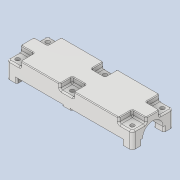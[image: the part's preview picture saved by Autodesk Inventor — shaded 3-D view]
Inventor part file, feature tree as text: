
AUTODESK INVENTOR PART (.ipt)
format: ipt  version: 2020.4 (Build 244396000, 396)  size: 785,920 bytes
history: native  units: mm
features: sketch x15, extrude x14, projected_geometry x10, fillet x3, other x1, mirror x1, boolean_combine x1
ambient origin geometry x8: Origin, YZ Plane, XZ Plane, XY Plane, X Axis, Y Axis, Z Axis, Center Point
bodies: Volumenkörper1 (feature_tree), Solid2 (feature_tree), Solid3 (feature_tree)
feature tree (45):
  extrude  "Extrusion1"  Depth=6.0mm
  other  "Spirale1"
  mirror  "Spiegeln1"
  extrude  "Extrusion5"  Depth=4.0mm
  extrude  "Extrusion6"  Depth=1.0mm
  boolean_combine  "Combine1"
  extrude  "Extrusion7"  Depth=10.0mm TaperAngle=0.0deg
  extrude  "Extrusion8"  Depth=7.0mm TaperAngle=0.0deg
  extrude  "Extrusion9"  Depth=24.0mm
  extrude  "Extrusion10"  Depth=12.0mm TaperAngle=0.0deg
  extrude  "Extrusion11"  Depth=4.0mm
  extrude  "Extrusion13"  Depth=77.15mm
  fillet  "Fillet2"  Radius=10.0mm
  fillet  "Fillet3"  Radius=77.15mm
  fillet  "Fillet4"  Radius=30.0mm
  extrude  "Extrusion14"  Depth=6.0mm
  extrude  "Extrusion15"  Depth=10.0mm TaperAngle=0.0deg
  extrude  "Extrusion16"  Depth=3.0mm
  extrude  "Extrusion17"  Depth=4.0mm
  extrude  "Extrusion19"  Depth=4.0mm
  sketch  "Skizze1"  dims[d0=6.0mm d1=11.0mm]
  sketch  "Skizze3"  dims[d2=36.0mm d3=0.0mm]
  projected_geometry  "Projizierte Kontur2"
  sketch  "Sketch7"  dims[d8=7.0mm d9=24.5mm d10=10.0mm d11=0.0mm d12=90.0deg d13=90.0deg d14=0.0mm d15=0.0mm d16=4.0mm]
  sketch  "Sketch8"  dims[d17=13.962634mm d18=1.0mm]
  sketch  "Sketch9"  dims[d19=0.1mm d32=10.0mm d33=0.0mm]
  projected_geometry  "Projected Loop4"
  sketch  "Sketch10"  dims[d34=7.0mm d35=100.0mm d36=0.0mm]
  sketch  "Sketch11"  dims[d37=82.0mm d38=0.0mm d39=24.0mm]
  projected_geometry  "Projected Loop5"
  projected_geometry  "Projected Loop6"
  sketch  "Sketch12"  dims[d40=30.0mm d41=12.0mm d42=0.0mm]
  sketch  "Sketch13"  dims[d43=3.0mm d44=4.0mm]
  projected_geometry  "Projected Loop7"
  projected_geometry  "Projected Loop8"
  sketch  "Sketch15"  dims[d45=4.0mm d46=20.0mm d48=22.0mm d49=20.0mm d51=84.0mm d54=10.0mm d55=0.0mm d56=77.15mm d57=30.0mm]
  sketch  "Sketch16"  dims[d62=4.0mm d63=0.0mm d64=6.0mm]
  projected_geometry  "Projected Loop10"
  sketch  "Sketch17"  dims[d65=10.0mm d66=0.0mm d67=10.0mm d68=0.0mm]
  projected_geometry  "Projected Loop11"
  projected_geometry  "Projected Loop12"
  sketch  "Sketch18"  dims[d76=3.0mm d77=3.0mm]
  sketch  "Sketch19"  dims[d78=4.0mm d79=48.0mm]
  sketch  "Sketch21"  dims[d80=46.0mm d81=4.0mm d85=7.0mm d86=6.9mm d87=3.5mm d88=7.0mm d89=6.9mm d90=3.5mm d91=10.0mm d92=10.0mm d93=10.0mm d94=10.0mm d95=10.0mm d96=10.0mm d97=10.0mm d98=10.0mm d99=10.0mm d100=10.0mm d101=10.0mm d102=10.0mm d103=4.0mm d104=0.0mm d105=1.0mm d106=1.0mm d107=2.0mm d108=0.5mm d109=6.5mm d110=2.1mm d111=0.0mm d112=6.5mm d113=2.1mm d114=0.0mm d115=180.0deg d116=6.9mm d117=6.9mm d118=6.9mm d119=6.9mm d120=12.0mm d121=0.2mm d122=0.0mm d123=15.0mm d124=0.2mm d125=0.0mm d126=7.9mm d127=0.0mm d128=7.9mm d129=0.0mm d132=3.0mm d133=0.0mm]
  projected_geometry  "Projected Loop13"
